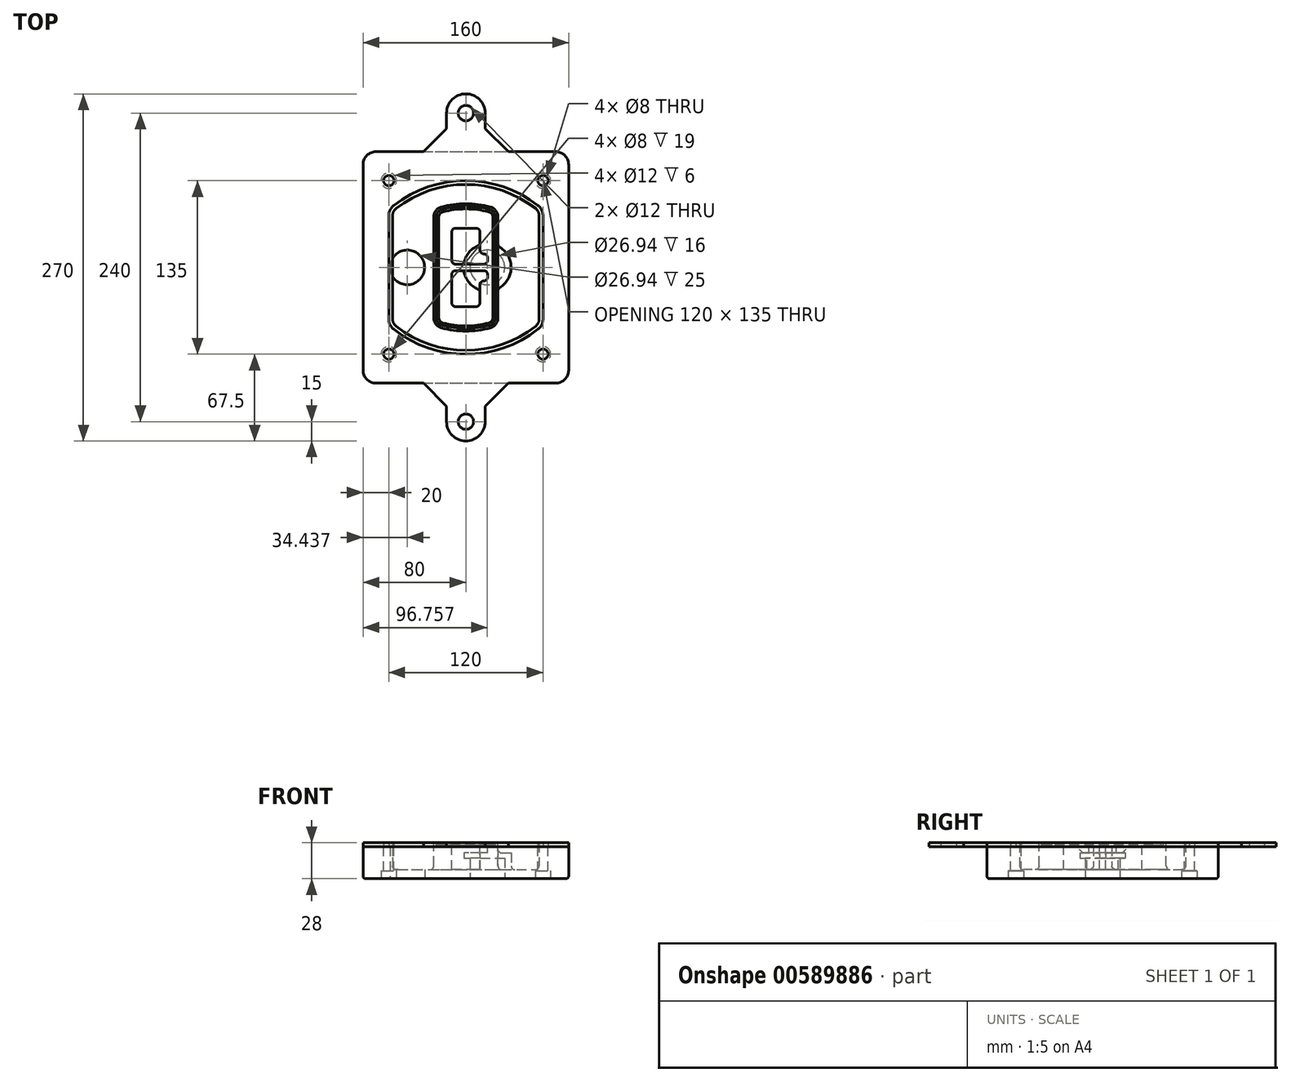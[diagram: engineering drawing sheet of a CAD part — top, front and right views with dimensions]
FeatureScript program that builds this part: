
annotation { "Feature Type Name" : "Feature", "Feature Type Description" : "" }
export const myFeature = defineFeature(function(context is Context, id is Id, definition is map)
    precondition{}
    {
        {
            var Q0;
            Q0=qCreatedBy(makeId("Top.planeOp"),FACE);
            var sketch = newSketch(context, id + "F0", { "sketchPlane" : qUnion([Q0])});
            skPoint(sketch, "E0.rect.middle", {"position": v(0, 0) * mm});
            skLineSegment(sketch, "E1.bottom", {"start": v(-70, -90) * mm, "end": v(70, -90) * mm});
            skLineSegment(sketch, "E1.top", {"start": v(-70, 90) * mm, "end": v(70, 90) * mm});
            skLineSegment(sketch, "E1.left", {"start": v(-80, -80) * mm, "end": v(-80, 80) * mm});
            skLineSegment(sketch, "E1.right", {"start": v(80, -80) * mm, "end": v(80, 80) * mm});
            skLineSegment(sketch, "E2", {"start": v(-80, 90) * mm, "end": v(80, -90) * mm, "construction": true});
            skLineSegment(sketch, "E3", {"start": v(80, 90) * mm, "end": v(-80, -90) * mm, "construction": true});
            skCircle(sketch, "E4", {"center": v(-60, 67.5) * mm, "radius": 4 * mm});
            skCircle(sketch, "E5", {"center": v(60, 67.5) * mm, "radius": 4 * mm});
            skCircle(sketch, "E6", {"center": v(60, -67.5) * mm, "radius": 4 * mm});
            skCircle(sketch, "E7", {"center": v(-60, -67.5) * mm, "radius": 4 * mm});
            skLineSegment(sketch, "E8", {"start": v(-60, 67.5) * mm, "end": v(60, 67.5) * mm, "construction": true});
            skLineSegment(sketch, "E9", {"start": v(60, 67.5) * mm, "end": v(60, -67.5) * mm, "construction": true});
            skLineSegment(sketch, "E10", {"start": v(60, -67.5) * mm, "end": v(-60, -67.5) * mm, "construction": true});
            skLineSegment(sketch, "E11", {"start": v(-60, -67.5) * mm, "end": v(-60, 67.5) * mm, "construction": true});
            skLineSegment(sketch, "E12", {"start": v(-60, 40.3) * mm, "end": v(-60, -40.3) * mm});
            skLineSegment(sketch, "E13", {"start": v(60, 40.3) * mm, "end": v(60, -40.3) * mm});
            skArc(sketch, "E14", {"start": v(56.15, 48.18) * mm, "mid": v(0, 67.5) * mm, "end": v(-56.15, 48.18) * mm});
            skArc(sketch, "E15", {"start": v(-56.15, -48.18) * mm, "mid": v(0, -67.5) * mm, "end": v(56.15, -48.18) * mm});
            skLineSegment(sketch, "E16", {"start": v(-60, 0) * mm, "end": v(60, 0) * mm, "construction": true});
            skPoint(sketch, "E17.visualSharp", {"position": v(-60, -45) * mm});
            skArc(sketch, "E17.filletArc", {"start": v(-60, -40.3) * mm, "mid": v(-58.99, -44.68) * mm, "end": v(-56.15, -48.18) * mm});
            skPoint(sketch, "E18.visualSharp", {"position": v(-60, 45) * mm});
            skArc(sketch, "E18.filletArc", {"start": v(-56.15, 48.18) * mm, "mid": v(-58.99, 44.68) * mm, "end": v(-60, 40.3) * mm});
            skPoint(sketch, "E19.visualSharp", {"position": v(60, 45) * mm});
            skArc(sketch, "E19.filletArc", {"start": v(60, 40.3) * mm, "mid": v(58.99, 44.68) * mm, "end": v(56.15, 48.18) * mm});
            skPoint(sketch, "E20.visualSharp", {"position": v(60, -45) * mm});
            skArc(sketch, "E20.filletArc", {"start": v(56.15, -48.18) * mm, "mid": v(58.99, -44.68) * mm, "end": v(60, -40.3) * mm});
            skPoint(sketch, "E21.visualSharp", {"position": v(-80, 90) * mm});
            skArc(sketch, "E21.filletArc", {"start": v(-70, 90) * mm, "mid": v(-77.07, 87.07) * mm, "end": v(-80, 80) * mm});
            skPoint(sketch, "E22.visualSharp", {"position": v(80, 90) * mm});
            skArc(sketch, "E22.filletArc", {"start": v(80, 80) * mm, "mid": v(77.07, 87.07) * mm, "end": v(70, 90) * mm});
            skPoint(sketch, "E23.visualSharp", {"position": v(80, -90) * mm});
            skArc(sketch, "E23.filletArc", {"start": v(70, -90) * mm, "mid": v(77.07, -87.07) * mm, "end": v(80, -80) * mm});
            skPoint(sketch, "E24.visualSharp", {"position": v(-80, -90) * mm});
            skArc(sketch, "E24.filletArc", {"start": v(-80, -80) * mm, "mid": v(-77.07, -87.07) * mm, "end": v(-70, -90) * mm});
            skArc(sketch, "E25.0", {"start": v(57, 40.3) * mm, "mid": v(56.3, 43.36) * mm, "end": v(54.3, 45.81) * mm});
            skLineSegment(sketch, "E25.1", {"start": v(57, 40.3) * mm, "end": v(57, -40.3) * mm});
            skArc(sketch, "E25.2", {"start": v(54.3, -45.81) * mm, "mid": v(56.3, -43.36) * mm, "end": v(57, -40.3) * mm});
            skArc(sketch, "E25.3", {"start": v(-54.3, -45.81) * mm, "mid": v(0, -64.5) * mm, "end": v(54.3, -45.81) * mm});
            skArc(sketch, "E25.4", {"start": v(-57, -40.3) * mm, "mid": v(-56.3, -43.36) * mm, "end": v(-54.3, -45.81) * mm});
            skArc(sketch, "E25.5", {"start": v(54.3, 45.81) * mm, "mid": v(0, 64.5) * mm, "end": v(-54.3, 45.81) * mm});
            skLineSegment(sketch, "E25.6", {"start": v(-57, 40.3) * mm, "end": v(-57, -40.3) * mm});
            skArc(sketch, "E25.7", {"start": v(-54.3, 45.81) * mm, "mid": v(-56.3, 43.36) * mm, "end": v(-57, 40.3) * mm});
            skArc(sketch, "E26.0", {"start": v(-58.62, 51.33) * mm, "mid": v(-62.58, 46.43) * mm, "end": v(-64, 40.3) * mm});
            skArc(sketch, "E26.1", {"start": v(58.62, 51.33) * mm, "mid": v(0, 71.5) * mm, "end": v(-58.62, 51.33) * mm});
            skArc(sketch, "E26.2", {"start": v(64, 40.3) * mm, "mid": v(62.58, 46.43) * mm, "end": v(58.62, 51.33) * mm});
            skLineSegment(sketch, "E26.3", {"start": v(64, 40.3) * mm, "end": v(64, -40.3) * mm});
            skArc(sketch, "E26.4", {"start": v(58.62, -51.33) * mm, "mid": v(62.58, -46.43) * mm, "end": v(64, -40.3) * mm});
            skLineSegment(sketch, "E26.5", {"start": v(-64, 40.3) * mm, "end": v(-64, -40.3) * mm});
            skArc(sketch, "E26.6", {"start": v(-58.62, -51.33) * mm, "mid": v(0, -71.5) * mm, "end": v(58.62, -51.33) * mm});
            skArc(sketch, "E26.7", {"start": v(-64, -40.3) * mm, "mid": v(-62.58, -46.43) * mm, "end": v(-58.62, -51.33) * mm});
            skSolve(sketch);
        }
        {
            var Q0;
            Q0=makeQuery(id+"F0.imprint","IMPRINT",FACE,{"disambiguationData":[TD([[makeQuery(id+"F0.imprint","IMPRINT",EDGE,{"derivedFrom":sQuery(id+"F0.wireOp",EDGE,"E1.bottom")}),1.0]])]});
            var Q1;
            Q1=makeQuery(id+"F0.imprint","IMPRINT",FACE,{"disambiguationData":[TD([[makeQuery(id+"F0.imprint","IMPRINT",EDGE,{"derivedFrom":sQuery(id+"F0.wireOp",EDGE,"E12")}),1.0]])]});
            var Q2;
            Q2=makeQuery(id+"F0.imprint","IMPRINT",FACE,{"disambiguationData":[TD([[makeQuery(id+"F0.imprint","IMPRINT",EDGE,{"derivedFrom":sQuery(id+"F0.wireOp",EDGE,"E25.0")}),1.0]])]});
            var Q3;
            Q3=makeQuery(id+"F0.imprint","IMPRINT",FACE,{"disambiguationData":[TD([[makeQuery(id+"F0.imprint","IMPRINT",EDGE,{"derivedFrom":sQuery(id+"F0.wireOp",EDGE,"E12")}),-1.0]])]});
            extrude(context, id + "F1", {"entities" : qUnion([Q0, Q1, Q2, Q3]), "oppositeDirection" : true, "depth" : 25 * mm});
        }
        {
            var Q0;
            Q0=makeQuery(id+"F0.imprint","IMPRINT",FACE,{"disambiguationData":[TD([[makeQuery(id+"F0.imprint","IMPRINT",EDGE,{"derivedFrom":sQuery(id+"F0.wireOp",EDGE,"E12")}),1.0]])]});
            extrude(context, id + "F2", {"entities" : qUnion([Q0]), "operationType" : NewBodyOperationType.ADD, "depth" : 3 * mm});
        }
        {
            var Q0;
            Q0=makeQuery(id+"F0.imprint","IMPRINT",FACE,{"disambiguationData":[TD([[makeQuery(id+"F0.imprint","IMPRINT",EDGE,{"derivedFrom":sQuery(id+"F0.wireOp",EDGE,"E25.0")}),1.0]])]});
            extrude(context, id + "F3", {"entities" : qUnion([Q0]), "operationType" : NewBodyOperationType.REMOVE, "oppositeDirection" : true, "depth" : 18 * mm});
        }
        {
            var Q0;
            Q0=makeQuery(id+"F2.opExtrude","CAP_FACE",FACE,{"disambiguationData":[OSD([sQuery(id+"F0.wireOp",EDGE,"E12"),sQuery(id+"F0.wireOp",EDGE,"E13"),sQuery(id+"F0.wireOp",EDGE,"E14"),sQuery(id+"F0.wireOp",EDGE,"E15"),sQuery(id+"F0.wireOp",EDGE,"E17.filletArc"),sQuery(id+"F0.wireOp",EDGE,"E18.filletArc"),sQuery(id+"F0.wireOp",EDGE,"E19.filletArc"),sQuery(id+"F0.wireOp",EDGE,"E20.filletArc"),sQuery(id+"F0.wireOp",EDGE,"E25.0"),sQuery(id+"F0.wireOp",EDGE,"E25.1"),sQuery(id+"F0.wireOp",EDGE,"E25.2"),sQuery(id+"F0.wireOp",EDGE,"E25.3"),sQuery(id+"F0.wireOp",EDGE,"E25.4"),sQuery(id+"F0.wireOp",EDGE,"E25.5"),sQuery(id+"F0.wireOp",EDGE,"E25.6"),sQuery(id+"F0.wireOp",EDGE,"E25.7")])],"isStart":false});
            var sketch = newSketch(context, id + "F4", { "sketchPlane" : qUnion([Q0])});
            skArc(sketch, "E27.0", {"start": v(-19.08, -46.97) * mm, "mid": v(0, -49.5) * mm, "end": v(19.08, -46.97) * mm});
            skArc(sketch, "E28.0", {"start": v(19.08, 46.97) * mm, "mid": v(0, 49.5) * mm, "end": v(-19.08, 46.97) * mm});
            skLineSegment(sketch, "E29", {"start": v(-25, 39.25) * mm, "end": v(-25, -39.25) * mm});
            skLineSegment(sketch, "E30", {"start": v(25, 39.25) * mm, "end": v(25, -39.25) * mm});
            skLineSegment(sketch, "E31", {"start": v(-25, 45.1) * mm, "end": v(25, 45.1) * mm, "construction": true});
            skLineSegment(sketch, "E32", {"start": v(-25, -45.1) * mm, "end": v(25, -45.1) * mm, "construction": true});
            skPoint(sketch, "E33.visualSharp", {"position": v(-25, 45.1) * mm});
            skArc(sketch, "E33.filletArc", {"start": v(-19.08, 46.97) * mm, "mid": v(-23.35, 44.11) * mm, "end": v(-25, 39.25) * mm});
            skPoint(sketch, "E34.visualSharp", {"position": v(25, 45.1) * mm});
            skArc(sketch, "E34.filletArc", {"start": v(25, 39.25) * mm, "mid": v(23.35, 44.11) * mm, "end": v(19.08, 46.97) * mm});
            skPoint(sketch, "E35.visualSharp", {"position": v(25, -45.1) * mm});
            skArc(sketch, "E35.filletArc", {"start": v(19.08, -46.97) * mm, "mid": v(23.35, -44.11) * mm, "end": v(25, -39.25) * mm});
            skPoint(sketch, "E36.visualSharp", {"position": v(-25, -45.1) * mm});
            skArc(sketch, "E36.filletArc", {"start": v(-25, -39.25) * mm, "mid": v(-23.35, -44.11) * mm, "end": v(-19.08, -46.97) * mm});
            skArc(sketch, "E37.0", {"start": v(54.3, 45.81) * mm, "mid": v(0, 64.5) * mm, "end": v(-54.3, 45.81) * mm});
            skArc(sketch, "E37.1", {"start": v(-54.3, 45.81) * mm, "mid": v(-56.3, 43.36) * mm, "end": v(-57, 40.3) * mm});
            skLineSegment(sketch, "E37.2", {"start": v(-57, 40.3) * mm, "end": v(-57, -40.3) * mm});
            skArc(sketch, "E37.3", {"start": v(-57, -40.3) * mm, "mid": v(-56.3, -43.36) * mm, "end": v(-54.3, -45.81) * mm});
            skArc(sketch, "E37.4", {"start": v(-54.3, -45.81) * mm, "mid": v(0, -64.5) * mm, "end": v(54.3, -45.81) * mm});
            skArc(sketch, "E37.5", {"start": v(54.3, -45.81) * mm, "mid": v(56.3, -43.36) * mm, "end": v(57, -40.3) * mm});
            skLineSegment(sketch, "E37.6", {"start": v(57, 40.3) * mm, "end": v(57, -40.3) * mm});
            skArc(sketch, "E37.7", {"start": v(57, 40.3) * mm, "mid": v(56.3, 43.36) * mm, "end": v(54.3, 45.81) * mm});
            skLineSegment(sketch, "E38.0", {"start": v(23, 39.25) * mm, "end": v(23, -39.25) * mm});
            skArc(sketch, "E38.1", {"start": v(18.56, -45.04) * mm, "mid": v(21.76, -42.9) * mm, "end": v(23, -39.25) * mm});
            skArc(sketch, "E38.2", {"start": v(-18.56, -45.04) * mm, "mid": v(0, -47.5) * mm, "end": v(18.56, -45.04) * mm});
            skArc(sketch, "E38.3", {"start": v(-23, -39.25) * mm, "mid": v(-21.76, -42.9) * mm, "end": v(-18.56, -45.04) * mm});
            skLineSegment(sketch, "E38.4", {"start": v(-23, 39.25) * mm, "end": v(-23, -39.25) * mm});
            skArc(sketch, "E38.5", {"start": v(23, 39.25) * mm, "mid": v(21.76, 42.9) * mm, "end": v(18.56, 45.04) * mm});
            skArc(sketch, "E38.6", {"start": v(-18.56, 45.04) * mm, "mid": v(-21.76, 42.9) * mm, "end": v(-23, 39.25) * mm});
            skArc(sketch, "E38.7", {"start": v(18.56, 45.04) * mm, "mid": v(0, 47.5) * mm, "end": v(-18.56, 45.04) * mm});
            skArc(sketch, "E39.0", {"start": v(21, 39.25) * mm, "mid": v(20.18, 41.68) * mm, "end": v(18.04, 43.1) * mm});
            skLineSegment(sketch, "E39.1", {"start": v(21, 39.25) * mm, "end": v(21, -39.25) * mm});
            skArc(sketch, "E39.2", {"start": v(18.04, -43.1) * mm, "mid": v(20.18, -41.68) * mm, "end": v(21, -39.25) * mm});
            skArc(sketch, "E39.3", {"start": v(-18.04, -43.1) * mm, "mid": v(0, -45.5) * mm, "end": v(18.04, -43.1) * mm});
            skArc(sketch, "E39.4", {"start": v(-21, -39.25) * mm, "mid": v(-20.18, -41.68) * mm, "end": v(-18.04, -43.1) * mm});
            skArc(sketch, "E39.5", {"start": v(18.04, 43.1) * mm, "mid": v(0, 45.5) * mm, "end": v(-18.04, 43.1) * mm});
            skLineSegment(sketch, "E39.6", {"start": v(-21, 39.25) * mm, "end": v(-21, -39.25) * mm});
            skArc(sketch, "E39.7", {"start": v(-18.04, 43.1) * mm, "mid": v(-20.18, 41.68) * mm, "end": v(-21, 39.25) * mm});
            skLineSegment(sketch, "E40", {"start": v(-25, 0) * mm, "end": v(25, 0) * mm, "construction": true});
            skLineSegment(sketch, "E41", {"start": v(-11, 5.5) * mm, "end": v(-11, 27.5) * mm});
            skLineSegment(sketch, "E42", {"start": v(-8, 30.5) * mm, "end": v(8, 30.5) * mm});
            skLineSegment(sketch, "E43", {"start": v(11, 27.5) * mm, "end": v(11, 13.5) * mm});
            skLineSegment(sketch, "E44", {"start": v(14, 10.5) * mm, "end": v(14, 10.5) * mm});
            skLineSegment(sketch, "E45", {"start": v(17, 7.5) * mm, "end": v(17, 5.5) * mm});
            skLineSegment(sketch, "E46", {"start": v(14, 2.5) * mm, "end": v(-8, 2.5) * mm});
            skPoint(sketch, "E47.visualSharp", {"position": v(-11, 30.5) * mm});
            skArc(sketch, "E47.filletArc", {"start": v(-8, 30.5) * mm, "mid": v(-10.12, 29.62) * mm, "end": v(-11, 27.5) * mm});
            skPoint(sketch, "E48.visualSharp", {"position": v(11, 30.5) * mm});
            skArc(sketch, "E48.filletArc", {"start": v(11, 27.5) * mm, "mid": v(10.12, 29.62) * mm, "end": v(8, 30.5) * mm});
            skPoint(sketch, "E49.visualSharp", {"position": v(11, 10.5) * mm});
            skArc(sketch, "E49.filletArc", {"start": v(11, 13.5) * mm, "mid": v(11.88, 11.38) * mm, "end": v(14, 10.5) * mm});
            skPoint(sketch, "E50.visualSharp", {"position": v(17, 10.5) * mm});
            skArc(sketch, "E50.filletArc", {"start": v(17, 7.5) * mm, "mid": v(16.12, 9.62) * mm, "end": v(14, 10.5) * mm});
            skPoint(sketch, "E51.visualSharp", {"position": v(17, 2.5) * mm});
            skArc(sketch, "E51.filletArc", {"start": v(14, 2.5) * mm, "mid": v(16.12, 3.38) * mm, "end": v(17, 5.5) * mm});
            skPoint(sketch, "E52.visualSharp", {"position": v(-11, 2.5) * mm});
            skArc(sketch, "E52.filletArc", {"start": v(-11, 5.5) * mm, "mid": v(-10.12, 3.38) * mm, "end": v(-8, 2.5) * mm});
            skLineSegment(sketch, "E53.0.MirrorCS", {"start": v(14, -2.5) * mm, "end": v(-8, -2.5) * mm});
            skArc(sketch, "E54.0.MirrorCS", {"start": v(-11, -5.5) * mm, "mid": v(-10.12, -3.38) * mm, "end": v(-8, -2.5) * mm});
            skLineSegment(sketch, "E55.0.MirrorCS", {"start": v(-11, -5.5) * mm, "end": v(-11, -27.5) * mm});
            skArc(sketch, "E56.0.MirrorCS", {"start": v(-8, -30.5) * mm, "mid": v(-10.12, -29.62) * mm, "end": v(-11, -27.5) * mm});
            skLineSegment(sketch, "E57.0.MirrorCS", {"start": v(-8, -30.5) * mm, "end": v(8, -30.5) * mm});
            skArc(sketch, "E58.0.MirrorCS", {"start": v(11, -27.5) * mm, "mid": v(10.12, -29.62) * mm, "end": v(8, -30.5) * mm});
            skLineSegment(sketch, "E59.0.MirrorCS", {"start": v(11, -27.5) * mm, "end": v(11, -13.5) * mm});
            skArc(sketch, "E60.0.MirrorCS", {"start": v(11, -13.5) * mm, "mid": v(11.88, -11.38) * mm, "end": v(14, -10.5) * mm});
            skArc(sketch, "E61.0.MirrorCS", {"start": v(17, -7.5) * mm, "mid": v(16.12, -9.62) * mm, "end": v(14, -10.5) * mm});
            skLineSegment(sketch, "E62.0.MirrorCS", {"start": v(17, -7.5) * mm, "end": v(17, -5.5) * mm});
            skArc(sketch, "E63.0.MirrorCS", {"start": v(14, -2.5) * mm, "mid": v(16.12, -3.38) * mm, "end": v(17, -5.5) * mm});
            skSolve(sketch);
        }
        {
            var Q0;
            Q0=makeQuery(id+"F4.imprint","IMPRINT",FACE,{"disambiguationData":[TD([[makeQuery(id+"F4.imprint","IMPRINT",EDGE,{"derivedFrom":sQuery(id+"F4.wireOp",EDGE,"E27.0")}),1.0]])]});
            var Q1;
            Q1=makeQuery(id+"F4.imprint","IMPRINT",FACE,{"disambiguationData":[TD([[makeQuery(id+"F4.imprint","IMPRINT",EDGE,{"derivedFrom":sQuery(id+"F4.wireOp",EDGE,"E38.0")}),-1.0]])]});
            var Q2;
            Q2=makeQuery(id+"F4.imprint","IMPRINT",FACE,{"disambiguationData":[TD([[makeQuery(id+"F4.imprint","IMPRINT",EDGE,{"derivedFrom":sQuery(id+"F4.wireOp",EDGE,"E39.0")}),1.0]])]});
            extrude(context, id + "F5", {"entities" : qUnion([Q0, Q1, Q2]), "operationType" : NewBodyOperationType.ADD, "endBound" : BoundingType.UP_TO_NEXT, "oppositeDirection" : true, "depth" : 25 * mm});
        }
        {
            var Q0;
            Q0=makeQuery(id+"F4.imprint","IMPRINT",FACE,{"disambiguationData":[TD([[makeQuery(id+"F4.imprint","IMPRINT",EDGE,{"derivedFrom":sQuery(id+"F4.wireOp",EDGE,"E38.0")}),-1.0]])]});
            extrude(context, id + "F6", {"entities" : qUnion([Q0]), "operationType" : NewBodyOperationType.REMOVE, "oppositeDirection" : true, "depth" : 2 * mm});
        }
        {
            var Q0;
            Q0=makeQuery(id+"F1.opExtrude","CAP_FACE",FACE,{"disambiguationData":[OSD([sQuery(id+"F0.wireOp",EDGE,"E1.bottom"),sQuery(id+"F0.wireOp",EDGE,"E1.top"),sQuery(id+"F0.wireOp",EDGE,"E1.left"),sQuery(id+"F0.wireOp",EDGE,"E1.right"),sQuery(id+"F0.wireOp",EDGE,"E4"),sQuery(id+"F0.wireOp",EDGE,"E5"),sQuery(id+"F0.wireOp",EDGE,"E6"),sQuery(id+"F0.wireOp",EDGE,"E7"),sQuery(id+"F0.wireOp",EDGE,"E21.filletArc"),sQuery(id+"F0.wireOp",EDGE,"E22.filletArc"),sQuery(id+"F0.wireOp",EDGE,"E23.filletArc"),sQuery(id+"F0.wireOp",EDGE,"E24.filletArc")])],"isStart":false});
            var sketch = newSketch(context, id + "F7", { "sketchPlane" : qUnion([Q0])});
            skCircle(sketch, "E64", {"center": v(16.76, 0) * mm, "radius": 13.47 * mm});
            skCircle(sketch, "E65", {"center": v(-45.56, 0) * mm, "radius": 13.47 * mm});
            skLineSegment(sketch, "E66", {"start": v(80, 0) * mm, "end": v(-80, 0) * mm});
            skCircle(sketch, "E67", {"center": v(16.76, 0) * mm, "radius": 18.47 * mm});
            skCircle(sketch, "E68", {"center": v(60, -67.5) * mm, "radius": 6 * mm});
            skCircle(sketch, "E69", {"center": v(-60, -67.5) * mm, "radius": 6 * mm});
            skCircle(sketch, "E70", {"center": v(-60, 67.5) * mm, "radius": 6 * mm});
            skCircle(sketch, "E71", {"center": v(60, 67.5) * mm, "radius": 6 * mm});
            skSolve(sketch);
        }
        {
            var Q0;
            {var subQ1=sQuery(id+"F7.wireOp",EDGE,"E66");var subQ4=sQuery(id+"F7.wireOp",EDGE,"E64");var subQ6=makeQuery(id+"F7.imprint","INTERSECT",VERTEX,{"disambiguationData":[OD(0.0)],"derivedFrom":[subQ4,subQ1]});Q0=makeQuery(id+"F7.imprint","IMPRINT",FACE,{"disambiguationData":[TD([[makeQuery(id+"F7.imprint","IMPRINT",EDGE,{"disambiguationData":[TD([[subQ6,-1.0]])],"derivedFrom":subQ4}),-1.0]])]});}
            var Q1;
            {var subQ0=sQuery(id+"F7.wireOp",EDGE,"E66");var subQ1=sQuery(id+"F7.wireOp",EDGE,"E64");var subQ3=makeQuery(id+"F7.imprint","INTERSECT",VERTEX,{"disambiguationData":[OD(0.0)],"derivedFrom":[subQ1,subQ0]});Q1=makeQuery(id+"F7.imprint","IMPRINT",FACE,{"disambiguationData":[TD([[makeQuery(id+"F7.imprint","IMPRINT",EDGE,{"disambiguationData":[TD([[subQ3,-1.0]])],"derivedFrom":subQ1}),1.0]])]});}
            var Q2;
            {var subQ0=sQuery(id+"F7.wireOp",EDGE,"E66");var subQ1=sQuery(id+"F7.wireOp",EDGE,"E64");var subQ3=makeQuery(id+"F7.imprint","INTERSECT",VERTEX,{"disambiguationData":[OD(0.0)],"derivedFrom":[subQ1,subQ0]});Q2=makeQuery(id+"F7.imprint","IMPRINT",FACE,{"disambiguationData":[TD([[makeQuery(id+"F7.imprint","IMPRINT",EDGE,{"disambiguationData":[TD([[subQ3,1.0]])],"derivedFrom":subQ1}),1.0]])]});}
            var Q3;
            {var subQ1=sQuery(id+"F7.wireOp",EDGE,"E66");var subQ4=sQuery(id+"F7.wireOp",EDGE,"E64");var subQ6=makeQuery(id+"F7.imprint","INTERSECT",VERTEX,{"disambiguationData":[OD(0.0)],"derivedFrom":[subQ4,subQ1]});Q3=makeQuery(id+"F7.imprint","IMPRINT",FACE,{"disambiguationData":[TD([[makeQuery(id+"F7.imprint","IMPRINT",EDGE,{"disambiguationData":[TD([[subQ6,1.0]])],"derivedFrom":subQ4}),-1.0]])]});}
            extrude(context, id + "F8", {"entities" : qUnion([Q0, Q1, Q2, Q3]), "operationType" : NewBodyOperationType.ADD, "oppositeDirection" : true, "depth" : 20 * mm});
        }
        {
            var Q0;
            {var subQ0=sQuery(id+"F7.wireOp",EDGE,"E66");var subQ1=sQuery(id+"F7.wireOp",EDGE,"E64");var subQ3=makeQuery(id+"F7.imprint","INTERSECT",VERTEX,{"disambiguationData":[OD(0.0)],"derivedFrom":[subQ1,subQ0]});Q0=makeQuery(id+"F7.imprint","IMPRINT",FACE,{"disambiguationData":[TD([[makeQuery(id+"F7.imprint","IMPRINT",EDGE,{"disambiguationData":[TD([[subQ3,-1.0]])],"derivedFrom":subQ1}),1.0]])]});}
            var Q1;
            {var subQ0=sQuery(id+"F7.wireOp",EDGE,"E66");var subQ1=sQuery(id+"F7.wireOp",EDGE,"E64");var subQ3=makeQuery(id+"F7.imprint","INTERSECT",VERTEX,{"disambiguationData":[OD(0.0)],"derivedFrom":[subQ1,subQ0]});Q1=makeQuery(id+"F7.imprint","IMPRINT",FACE,{"disambiguationData":[TD([[makeQuery(id+"F7.imprint","IMPRINT",EDGE,{"disambiguationData":[TD([[subQ3,1.0]])],"derivedFrom":subQ1}),1.0]])]});}
            extrude(context, id + "F9", {"entities" : qUnion([Q0, Q1]), "operationType" : NewBodyOperationType.REMOVE, "oppositeDirection" : true, "depth" : 16 * mm});
        }
        {
            var Q0;
            {var subQ0=sQuery(id+"F7.wireOp",EDGE,"E66");var subQ1=sQuery(id+"F7.wireOp",EDGE,"E65");var subQ3=makeQuery(id+"F7.imprint","INTERSECT",VERTEX,{"disambiguationData":[OD(0.0)],"derivedFrom":[subQ1,subQ0]});Q0=makeQuery(id+"F7.imprint","IMPRINT",FACE,{"disambiguationData":[TD([[makeQuery(id+"F7.imprint","IMPRINT",EDGE,{"disambiguationData":[TD([[subQ3,-1.0]])],"derivedFrom":subQ1}),1.0]])]});}
            var Q1;
            {var subQ0=sQuery(id+"F7.wireOp",EDGE,"E66");var subQ1=sQuery(id+"F7.wireOp",EDGE,"E65");var subQ3=makeQuery(id+"F7.imprint","INTERSECT",VERTEX,{"disambiguationData":[OD(0.0)],"derivedFrom":[subQ1,subQ0]});Q1=makeQuery(id+"F7.imprint","IMPRINT",FACE,{"disambiguationData":[TD([[makeQuery(id+"F7.imprint","IMPRINT",EDGE,{"disambiguationData":[TD([[subQ3,1.0]])],"derivedFrom":subQ1}),1.0]])]});}
            extrude(context, id + "F10", {"entities" : qUnion([Q0, Q1]), "operationType" : NewBodyOperationType.REMOVE, "oppositeDirection" : true, "depth" : 25 * mm});
        }
        {
            var Q0;
            Q0=makeQuery(id+"F7.imprint","IMPRINT",FACE,{"disambiguationData":[TD([[makeQuery(id+"F7.imprint","IMPRINT",EDGE,{"derivedFrom":sQuery(id+"F7.wireOp",EDGE,"E68")}),1.0]])]});
            var Q1;
            Q1=makeQuery(id+"F7.imprint","IMPRINT",FACE,{"disambiguationData":[TD([[makeQuery(id+"F7.imprint","IMPRINT",EDGE,{"derivedFrom":makeQuery(id+"F1.opExtrude","CAP_EDGE",EDGE,{"disambiguationData":[OSD([sQuery(id+"F0.wireOp",EDGE,"E5")])],"isStart":false})}),-1.0]])]});
            var Q2;
            Q2=makeQuery(id+"F7.imprint","IMPRINT",FACE,{"disambiguationData":[TD([[makeQuery(id+"F7.imprint","IMPRINT",EDGE,{"derivedFrom":sQuery(id+"F7.wireOp",EDGE,"E69")}),1.0]])]});
            var Q3;
            Q3=makeQuery(id+"F7.imprint","IMPRINT",FACE,{"disambiguationData":[TD([[makeQuery(id+"F7.imprint","IMPRINT",EDGE,{"derivedFrom":makeQuery(id+"F1.opExtrude","CAP_EDGE",EDGE,{"disambiguationData":[OSD([sQuery(id+"F0.wireOp",EDGE,"E4")])],"isStart":false})}),-1.0]])]});
            var Q4;
            Q4=makeQuery(id+"F7.imprint","IMPRINT",FACE,{"disambiguationData":[TD([[makeQuery(id+"F7.imprint","IMPRINT",EDGE,{"derivedFrom":sQuery(id+"F7.wireOp",EDGE,"E70")}),1.0]])]});
            var Q5;
            Q5=makeQuery(id+"F7.imprint","IMPRINT",FACE,{"disambiguationData":[TD([[makeQuery(id+"F7.imprint","IMPRINT",EDGE,{"derivedFrom":makeQuery(id+"F1.opExtrude","CAP_EDGE",EDGE,{"disambiguationData":[OSD([sQuery(id+"F0.wireOp",EDGE,"E7")])],"isStart":false})}),-1.0]])]});
            var Q6;
            Q6=makeQuery(id+"F7.imprint","IMPRINT",FACE,{"disambiguationData":[TD([[makeQuery(id+"F7.imprint","IMPRINT",EDGE,{"derivedFrom":sQuery(id+"F7.wireOp",EDGE,"E71")}),1.0]])]});
            var Q7;
            Q7=makeQuery(id+"F7.imprint","IMPRINT",FACE,{"disambiguationData":[TD([[makeQuery(id+"F7.imprint","IMPRINT",EDGE,{"derivedFrom":makeQuery(id+"F1.opExtrude","CAP_EDGE",EDGE,{"disambiguationData":[OSD([sQuery(id+"F0.wireOp",EDGE,"E6")])],"isStart":false})}),-1.0]])]});
            extrude(context, id + "F11", {"entities" : qUnion([Q0, Q1, Q2, Q3, Q4, Q5, Q6, Q7]), "operationType" : NewBodyOperationType.REMOVE, "oppositeDirection" : true, "depth" : 6 * mm});
        }
        {
            var Q0;
            Q0=makeQuery(id+"F9.boolean.opBoolean","COPY",FACE,{"derivedFrom":makeQuery(id+"F9.opExtrude","CAP_FACE",FACE,{"disambiguationData":[OSD([sQuery(id+"F7.wireOp",EDGE,"E64")])],"isStart":false})});
            var sketch = newSketch(context, id + "F12", { "sketchPlane" : qUnion([Q0])});
            skArc(sketch, "E72.0", {"start": v(11, 17.55) * mm, "mid": v(2.57, 11.82) * mm, "end": v(-1.54, 2.5) * mm});
            skArc(sketch, "E72.1", {"start": v(-1.54, -2.5) * mm, "mid": v(2.57, -11.82) * mm, "end": v(11, -17.55) * mm});
            skLineSegment(sketch, "E73", {"start": v(-1.54, -2.5) * mm, "end": v(14, -2.5) * mm});
            skLineSegment(sketch, "E74.0", {"start": v(14, 2.5) * mm, "end": v(-1.54, 2.5) * mm});
            skArc(sketch, "E74.1", {"start": v(14, 2.5) * mm, "mid": v(16.12, 3.38) * mm, "end": v(17, 5.5) * mm});
            skLineSegment(sketch, "E74.2", {"start": v(17, 7.5) * mm, "end": v(17, 5.5) * mm});
            skArc(sketch, "E74.3", {"start": v(17, 7.5) * mm, "mid": v(16.12, 9.62) * mm, "end": v(14, 10.5) * mm});
            skArc(sketch, "E74.4", {"start": v(11, 13.5) * mm, "mid": v(11.88, 11.38) * mm, "end": v(14, 10.5) * mm});
            skLineSegment(sketch, "E74.5", {"start": v(11, 17.55) * mm, "end": v(11, 13.5) * mm});
            skLineSegment(sketch, "E74.7", {"start": v(14, -2.5) * mm, "end": v(-1.54, -2.5) * mm});
            skArc(sketch, "E74.8", {"start": v(14, -2.5) * mm, "mid": v(16.12, -3.38) * mm, "end": v(17, -5.5) * mm});
            skLineSegment(sketch, "E74.9", {"start": v(17, -7.5) * mm, "end": v(17, -5.5) * mm});
            skArc(sketch, "E74.10", {"start": v(17, -7.5) * mm, "mid": v(16.12, -9.62) * mm, "end": v(14, -10.5) * mm});
            skArc(sketch, "E74.11", {"start": v(11, -13.5) * mm, "mid": v(11.88, -11.38) * mm, "end": v(14, -10.5) * mm});
            skLineSegment(sketch, "E74.12", {"start": v(11, -17.55) * mm, "end": v(11, -13.5) * mm});
            skPoint(sketch, "E75.orphan", {"position": v(11, -27.5) * mm});
            skPoint(sketch, "E76.orphan", {"position": v(-8, -2.5) * mm});
            skPoint(sketch, "E77.orphan", {"position": v(-8, 2.5) * mm});
            skPoint(sketch, "E78.orphan", {"position": v(11, 27.5) * mm});
            skSolve(sketch);
        }
        {
            var Q0;
            {var subQ7=sQuery(id+"F12.wireOp",EDGE,"E72.0");var subQ14=sQuery(id+"F12.wireOp",EDGE,"E72.1");var subQ16=sQuery(id+"F12.wireOp",EDGE,"E74.1");var subQ18=sQuery(id+"F12.wireOp",EDGE,"E74.8");Q0=qUnion([makeQuery(id+"F12.imprint","IMPRINT",FACE,{"disambiguationData":[TD([[makeQuery(id+"F12.imprint","IMPRINT",EDGE,{"derivedFrom":subQ7}),1.0]])]}),makeQuery(id+"F12.imprint","IMPRINT",FACE,{"disambiguationData":[TD([[makeQuery(id+"F12.imprint","IMPRINT",EDGE,{"derivedFrom":subQ14}),1.0]])]}),makeQuery(id+"F12.imprint","IMPRINT",FACE,{"disambiguationData":[TD([[makeQuery(id+"F12.imprint","IMPRINT",EDGE,{"derivedFrom":subQ16}),1.0]])]}),makeQuery(id+"F12.imprint","IMPRINT",FACE,{"disambiguationData":[TD([[makeQuery(id+"F12.imprint","IMPRINT",EDGE,{"derivedFrom":subQ18}),-1.0]])]})]);}
            var Q1;
            Q1=makeQuery(id+"F5.boolean.opBoolean","SPLIT",FACE,{"disambiguationData":[TD([makeQuery(id+"F5.opExtrude","SWEPT_FACE",FACE,{"disambiguationData":[OSD([sQuery(id+"F4.wireOp",EDGE,"E41")])]})])],"derivedFrom":makeQuery(id+"F3.boolean.opBoolean","COPY",FACE,{"derivedFrom":makeQuery(id+"F3.opExtrude","CAP_FACE",FACE,{"disambiguationData":[OSD([sQuery(id+"F0.wireOp",EDGE,"E25.0"),sQuery(id+"F0.wireOp",EDGE,"E25.1"),sQuery(id+"F0.wireOp",EDGE,"E25.2"),sQuery(id+"F0.wireOp",EDGE,"E25.3"),sQuery(id+"F0.wireOp",EDGE,"E25.4"),sQuery(id+"F0.wireOp",EDGE,"E25.5"),sQuery(id+"F0.wireOp",EDGE,"E25.6"),sQuery(id+"F0.wireOp",EDGE,"E25.7")])],"isStart":false})})});
            extrude(context, id + "F13", {"entities" : qUnion([Q0]), "operationType" : NewBodyOperationType.REMOVE, "endBound" : BoundingType.UP_TO_SURFACE, "endBoundEntityFace" : qUnion([Q1]), "depth" : 25 * mm});
        }
        {
            var Q0;
            Q0=makeQuery(id+"F3.boolean.opBoolean","COPY",EDGE,{"derivedFrom":makeQuery(id+"F3.opExtrude","CAP_EDGE",EDGE,{"disambiguationData":[OSD([sQuery(id+"F0.wireOp",EDGE,"E25.6")])],"isStart":false})});
            var Q1;
            Q1=makeQuery(id+"F8.boolean.opBoolean","INTERSECT",EDGE,{"derivedFrom":[makeQuery(id+"F5.opExtrude","SWEPT_FACE",FACE,{"disambiguationData":[OSD([sQuery(id+"F4.wireOp",EDGE,"E30")])]}),makeQuery(id+"F8.opExtrude","CAP_FACE",FACE,{"disambiguationData":[OSD([sQuery(id+"F7.wireOp",EDGE,"E67")])],"isStart":false})]});
            var Q2;
            Q2=makeQuery(id+"F8.boolean.opBoolean","INTERSECT",EDGE,{"disambiguationData":[OD(1.0)],"derivedFrom":[makeQuery(id+"F5.opExtrude","SWEPT_FACE",FACE,{"disambiguationData":[OSD([sQuery(id+"F4.wireOp",EDGE,"E30")])]}),makeQuery(id+"F8.opExtrude","SWEPT_FACE",FACE,{"disambiguationData":[OSD([sQuery(id+"F7.wireOp",EDGE,"E67")])]})]});
            var Q3;
            {var subQ0=sQuery(id+"F4.wireOp",EDGE,"E30");Q3=makeQuery(id+"F8.boolean.opBoolean","SPLIT",EDGE,{"disambiguationData":[TD([makeQuery(id+"F5.opExtrude","SWEPT_FACE",FACE,{"disambiguationData":[OSD([sQuery(id+"F4.wireOp",EDGE,"E35.filletArc")])]})])],"derivedFrom":makeQuery(id+"F5.opExtrude","CAP_EDGE",EDGE,{"disambiguationData":[OSD([subQ0])],"isStart":false})});}
            var Q4;
            {var subQ0=sQuery(id+"F0.wireOp",EDGE,"E25.7");var subQ1=sQuery(id+"F0.wireOp",EDGE,"E25.1");var subQ2=sQuery(id+"F0.wireOp",EDGE,"E25.6");var subQ3=sQuery(id+"F0.wireOp",EDGE,"E25.5");var subQ4=sQuery(id+"F0.wireOp",EDGE,"E25.4");var subQ5=sQuery(id+"F0.wireOp",EDGE,"E25.0");var subQ6=sQuery(id+"F0.wireOp",EDGE,"E25.2");var subQ7=sQuery(id+"F0.wireOp",EDGE,"E25.3");Q4=makeQuery(id+"F8.boolean.opBoolean","INTERSECT",EDGE,{"derivedFrom":[makeQuery(id+"F5.boolean.opBoolean","SPLIT",FACE,{"disambiguationData":[TD([makeQuery(id+"F2.opExtrude","SWEPT_FACE",FACE,{"disambiguationData":[OSD([subQ5])]})])],"derivedFrom":makeQuery(id+"F3.boolean.opBoolean","COPY",FACE,{"derivedFrom":makeQuery(id+"F3.opExtrude","CAP_FACE",FACE,{"disambiguationData":[OSD([subQ5,subQ1,subQ6,subQ7,subQ4,subQ3,subQ2,subQ0])],"isStart":false})})}),makeQuery(id+"F8.opExtrude","SWEPT_FACE",FACE,{"disambiguationData":[OSD([sQuery(id+"F7.wireOp",EDGE,"E67")])]})]});}
            var Q5;
            Q5=makeQuery(id+"F8.boolean.opBoolean","INTERSECT",EDGE,{"disambiguationData":[OD(0.0)],"derivedFrom":[makeQuery(id+"F5.opExtrude","SWEPT_FACE",FACE,{"disambiguationData":[OSD([sQuery(id+"F4.wireOp",EDGE,"E30")])]}),makeQuery(id+"F8.opExtrude","SWEPT_FACE",FACE,{"disambiguationData":[OSD([sQuery(id+"F7.wireOp",EDGE,"E67")])]})]});
            fillet(context, id + "F14", {"entities" : qUnion([Q0, Q1, Q2, Q3, Q4, Q5]), "radius" : 3 * mm, "tangentPropagation" : true, "allowEdgeOverflow" : false});
        }
        {
            var Q0;
            Q0=makeQuery(id+"F1.opExtrude","CAP_EDGE",EDGE,{"disambiguationData":[OSD([sQuery(id+"F0.wireOp",EDGE,"E1.bottom")])],"isStart":false});
            fillet(context, id + "F15", {"entities" : qUnion([Q0]), "radius" : 2 * mm, "tangentPropagation" : true, "allowEdgeOverflow" : false});
        }
        {
            var Q0;
            {var subQ0=sQuery(id+"F0.wireOp",EDGE,"E21.filletArc");var subQ1=sQuery(id+"F0.wireOp",EDGE,"E7");var subQ2=sQuery(id+"F0.wireOp",EDGE,"E6");var subQ3=sQuery(id+"F0.wireOp",EDGE,"E5");var subQ4=sQuery(id+"F0.wireOp",EDGE,"E4");var subQ5=sQuery(id+"F0.wireOp",EDGE,"E22.filletArc");var subQ6=sQuery(id+"F0.wireOp",EDGE,"E1.bottom");var subQ7=sQuery(id+"F0.wireOp",EDGE,"E1.right");var subQ8=sQuery(id+"F0.wireOp",EDGE,"E1.top");var subQ9=sQuery(id+"F0.wireOp",EDGE,"E1.left");var subQ10=sQuery(id+"F0.wireOp",EDGE,"E23.filletArc");var subQ11=sQuery(id+"F0.wireOp",EDGE,"E24.filletArc");Q0=makeQuery(id+"F2.boolean.opBoolean","SPLIT",FACE,{"disambiguationData":[TD([makeQuery(id+"F1.opExtrude","SWEPT_FACE",FACE,{"disambiguationData":[OSD([subQ6])]})])],"derivedFrom":makeQuery(id+"F1.opExtrude","CAP_FACE",FACE,{"disambiguationData":[OSD([subQ6,subQ8,subQ9,subQ7,subQ4,subQ3,subQ2,subQ1,subQ0,subQ5,subQ10,subQ11])],"isStart":true})});}
            var sketch = newSketch(context, id + "F16", { "sketchPlane" : qUnion([Q0])});
            skLineSegment(sketch, "E79", {"start": v(0, 90) * mm, "end": v(0, 120) * mm, "construction": true});
            skCircle(sketch, "E80", {"center": v(0, 120) * mm, "radius": 6 * mm});
            skArc(sketch, "E81", {"start": v(15, 120) * mm, "mid": v(0, 135) * mm, "end": v(-15, 120) * mm});
            skLineSegment(sketch, "E82", {"start": v(-15, 120) * mm, "end": v(-15, 108) * mm});
            skLineSegment(sketch, "E83", {"start": v(15, 120) * mm, "end": v(15, 108) * mm});
            skLineSegment(sketch, "E84", {"start": v(15, 108) * mm, "end": v(33, 90) * mm});
            skLineSegment(sketch, "E85", {"start": v(-33, 90) * mm, "end": v(-15, 108) * mm});
            skLineSegment(sketch, "E86", {"start": v(74.23, 0) * mm, "end": v(-80, 0) * mm, "construction": true});
            skLineSegment(sketch, "E87.MirrorCS", {"start": v(15, -120) * mm, "end": v(15, -108) * mm});
            skLineSegment(sketch, "E88.MirrorCS", {"start": v(-15, -120) * mm, "end": v(-15, -108) * mm});
            skLineSegment(sketch, "E89.MirrorCS", {"start": v(-33, -90) * mm, "end": v(-15, -108) * mm});
            skLineSegment(sketch, "E90.MirrorCS", {"start": v(15, -108) * mm, "end": v(33, -90) * mm});
            skLineSegment(sketch, "E91.MirrorCS", {"start": v(0, -90) * mm, "end": v(0, -120) * mm, "construction": true});
            skArc(sketch, "E92.MirrorCS", {"start": v(15, -120) * mm, "mid": v(0, -135) * mm, "end": v(-15, -120) * mm});
            skCircle(sketch, "E93.MirrorC", {"center": v(0, -120) * mm, "radius": 6 * mm});
            skLineSegment(sketch, "E94.0", {"start": v(80, -80) * mm, "end": v(80, 80) * mm});
            skArc(sketch, "E94.1", {"start": v(80, 80) * mm, "mid": v(77.07, 87.07) * mm, "end": v(70, 90) * mm});
            skLineSegment(sketch, "E94.2", {"start": v(-70, 90) * mm, "end": v(70, 90) * mm});
            skArc(sketch, "E94.3", {"start": v(-70, 90) * mm, "mid": v(-77.07, 87.07) * mm, "end": v(-80, 80) * mm});
            skLineSegment(sketch, "E94.4", {"start": v(-80, -80) * mm, "end": v(-80, 80) * mm});
            skArc(sketch, "E94.5", {"start": v(-80, -80) * mm, "mid": v(-77.07, -87.07) * mm, "end": v(-70, -90) * mm});
            skLineSegment(sketch, "E94.6", {"start": v(-70, -90) * mm, "end": v(70, -90) * mm});
            skArc(sketch, "E94.7", {"start": v(70, -90) * mm, "mid": v(77.07, -87.07) * mm, "end": v(80, -80) * mm});
            skArc(sketch, "E94.8", {"start": v(-56.15, -48.18) * mm, "mid": v(0, -67.5) * mm, "end": v(56.15, -48.18) * mm});
            skArc(sketch, "E94.9", {"start": v(56.15, -48.18) * mm, "mid": v(58.99, -44.68) * mm, "end": v(60, -40.3) * mm});
            skLineSegment(sketch, "E94.10", {"start": v(60, 40.3) * mm, "end": v(60, -40.3) * mm});
            skArc(sketch, "E94.11", {"start": v(60, 40.3) * mm, "mid": v(58.99, 44.68) * mm, "end": v(56.15, 48.18) * mm});
            skArc(sketch, "E94.12", {"start": v(56.15, 48.18) * mm, "mid": v(0, 67.5) * mm, "end": v(-56.15, 48.18) * mm});
            skArc(sketch, "E94.13", {"start": v(-56.15, 48.18) * mm, "mid": v(-58.99, 44.68) * mm, "end": v(-60, 40.3) * mm});
            skLineSegment(sketch, "E94.14", {"start": v(-60, 40.3) * mm, "end": v(-60, -40.3) * mm});
            skArc(sketch, "E94.15", {"start": v(-60, -40.3) * mm, "mid": v(-58.99, -44.68) * mm, "end": v(-56.15, -48.18) * mm});
            skCircle(sketch, "E95.0", {"center": v(-60, -67.5) * mm, "radius": 4 * mm});
            skCircle(sketch, "E95.1", {"center": v(60, -67.5) * mm, "radius": 4 * mm});
            skCircle(sketch, "E95.2", {"center": v(60, 67.5) * mm, "radius": 4 * mm});
            skCircle(sketch, "E95.3", {"center": v(-60, 67.5) * mm, "radius": 4 * mm});
            skSolve(sketch);
        }
        {
            var Q0;
            Q0=makeQuery(id+"F16.imprint","IMPRINT",FACE,{"disambiguationData":[TD([[makeQuery(id+"F16.imprint","IMPRINT",EDGE,{"derivedFrom":sQuery(id+"F16.wireOp",EDGE,"E80")}),-1.0]])]});
            var Q1;
            Q1=makeQuery(id+"F16.imprint","IMPRINT",FACE,{"disambiguationData":[TD([[makeQuery(id+"F16.imprint","IMPRINT",EDGE,{"derivedFrom":sQuery(id+"F16.wireOp",EDGE,"E94.0")}),1.0]])]});
            var Q2;
            Q2=makeQuery(id+"F16.imprint","IMPRINT",FACE,{"disambiguationData":[TD([[makeQuery(id+"F16.imprint","IMPRINT",EDGE,{"derivedFrom":sQuery(id+"F16.wireOp",EDGE,"E87.MirrorCS")}),1.0]])]});
            var Q3;
            Q3=makeQuery(id+"F2.opExtrude","CAP_FACE",FACE,{"disambiguationData":[OSD([sQuery(id+"F0.wireOp",EDGE,"E12"),sQuery(id+"F0.wireOp",EDGE,"E13"),sQuery(id+"F0.wireOp",EDGE,"E14"),sQuery(id+"F0.wireOp",EDGE,"E15"),sQuery(id+"F0.wireOp",EDGE,"E17.filletArc"),sQuery(id+"F0.wireOp",EDGE,"E18.filletArc"),sQuery(id+"F0.wireOp",EDGE,"E19.filletArc"),sQuery(id+"F0.wireOp",EDGE,"E20.filletArc"),sQuery(id+"F0.wireOp",EDGE,"E25.0"),sQuery(id+"F0.wireOp",EDGE,"E25.1"),sQuery(id+"F0.wireOp",EDGE,"E25.2"),sQuery(id+"F0.wireOp",EDGE,"E25.3"),sQuery(id+"F0.wireOp",EDGE,"E25.4"),sQuery(id+"F0.wireOp",EDGE,"E25.5"),sQuery(id+"F0.wireOp",EDGE,"E25.6"),sQuery(id+"F0.wireOp",EDGE,"E25.7")])],"isStart":false});
            extrude(context, id + "F17", {"entities" : qUnion([Q0, Q1, Q2]), "endBound" : BoundingType.UP_TO_SURFACE, "depth" : 25 * mm, "endBoundEntityFace" : qUnion([Q3]), "offsetDistance" : 25 * mm});
        }
    });
